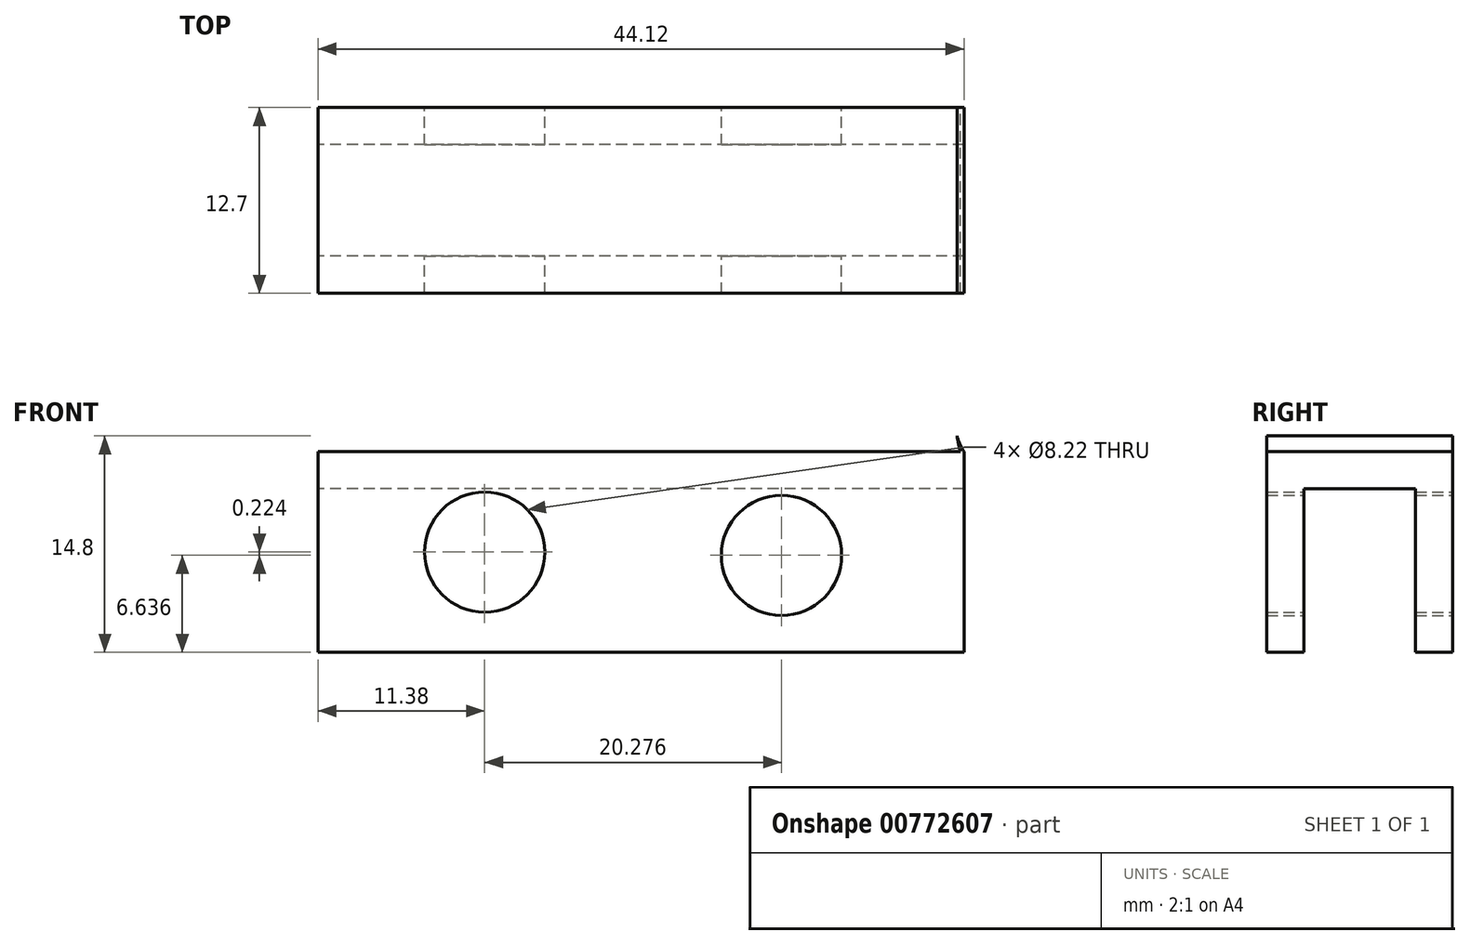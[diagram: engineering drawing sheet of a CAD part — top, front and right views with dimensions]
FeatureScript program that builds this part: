
annotation { "Feature Type Name" : "Feature", "Feature Type Description" : "" }
export const myFeature = defineFeature(function(context is Context, id is Id, definition is map)
    precondition{}
    {
        {
            var Q0;
            Q0=qCreatedBy(makeId("Front.planeOp"),FACE);
            var sketch = newSketch(context, id + "F0", { "sketchPlane" : qUnion([Q0])});
            skLineSegment(sketch, "E0.top", {"start": v(-62.7, -6.86) * mm, "end": v(-106.82, -6.86) * mm});
            skLineSegment(sketch, "E0.left", {"start": v(-62.7, 6.86) * mm, "end": v(-62.7, -6.86) * mm});
            skLineSegment(sketch, "E0.right", {"start": v(-106.82, 6.86) * mm, "end": v(-106.82, -6.86) * mm});
            skPoint(sketch, "E0.middle", {"position": v(-84.76, 0) * mm});
            skFitSpline(sketch, "E1", {"points": [v(-62.7, 6.86) * mm, v(34.46, 6.86) * mm], "startDerivative": vector(-28.15, 47.5) * mm, "endDerivative": vector(44.82, -144.27) * mm});
            skLineSegment(sketch, "E2", {"start": v(34.46, 6.86) * mm, "end": v(36.14, 11.12) * mm});
            skLineSegment(sketch, "E3", {"start": v(-80.52, 6.86) * mm, "end": v(-58.36, 27.07) * mm});
            skFitSpline(sketch, "E4.trimOffspring", {"points": [v(-62.95, 6.86) * mm, v(36.14, 11.12) * mm], "startDerivative": vector(-30.68, 132.69) * mm, "endDerivative": vector(13.72, -133.6) * mm});
            skLineSegment(sketch, "E5", {"start": v(-62.7, 6.86) * mm, "end": v(-106.82, 6.86) * mm});
            skCircle(sketch, "E6", {"center": v(-95.44, 0) * mm, "radius": 4.1 * mm});
            skCircle(sketch, "E7", {"center": v(-75.16, -0.22) * mm, "radius": 4.1 * mm});
            skSolve(sketch);
        }
        {
            var Q0;
            {var subQ1=sQuery(id+"F0.wireOp",EDGE,"E1");Q0=makeQuery(id+"F0.imprint","IMPRINT",FACE,{"disambiguationData":[TD([[makeQuery(id+"F0.imprint","IMPRINT",EDGE,{"derivedFrom":subQ1}),1.0]])]});}
            var Q1;
            Q1=makeQuery(id+"F0.imprint","IMPRINT",FACE,{"disambiguationData":[TD([[makeQuery(id+"F0.imprint","IMPRINT",EDGE,{"derivedFrom":sQuery(id+"F0.wireOp",EDGE,"E0.top")}),-1.0]])]});
            extrude(context, id + "F1", {"entities" : qUnion([Q0, Q1]), "endBound" : BoundingType.SYMMETRIC, "depth" : 12.7 * mm, "offsetDistance" : 25.4 * mm});
        }
        {
            var Q0;
            Q0=makeQuery(id+"F1.opExtrude","SWEPT_FACE",FACE,{"disambiguationData":[OSD([sQuery(id+"F0.wireOp",EDGE,"E6")])]});
            var Q1;
            Q1=makeQuery(id+"F1.opExtrude","SWEPT_FACE",FACE,{"disambiguationData":[OSD([sQuery(id+"F0.wireOp",EDGE,"E0.top")])]});
            var Q2;
            Q2=makeQuery(id+"F1.opExtrude","SWEPT_FACE",FACE,{"disambiguationData":[OSD([sQuery(id+"F0.wireOp",EDGE,"E7")])]});
            var Q3;
            Q3=makeQuery(id+"F1.opExtrude","SWEPT_FACE",FACE,{"disambiguationData":[OSD([sQuery(id+"F0.wireOp",EDGE,"E0.left")])]});
            var Q4;
            Q4=makeQuery(id+"F1.opExtrude","SWEPT_FACE",FACE,{"disambiguationData":[OSD([sQuery(id+"F0.wireOp",EDGE,"E0.right")])]});
            shell(context, id + "F2", {"entities" : qUnion([Q0, Q1, Q2, Q3, Q4]), "thickness" : 2.54 * mm});
        }
    });
